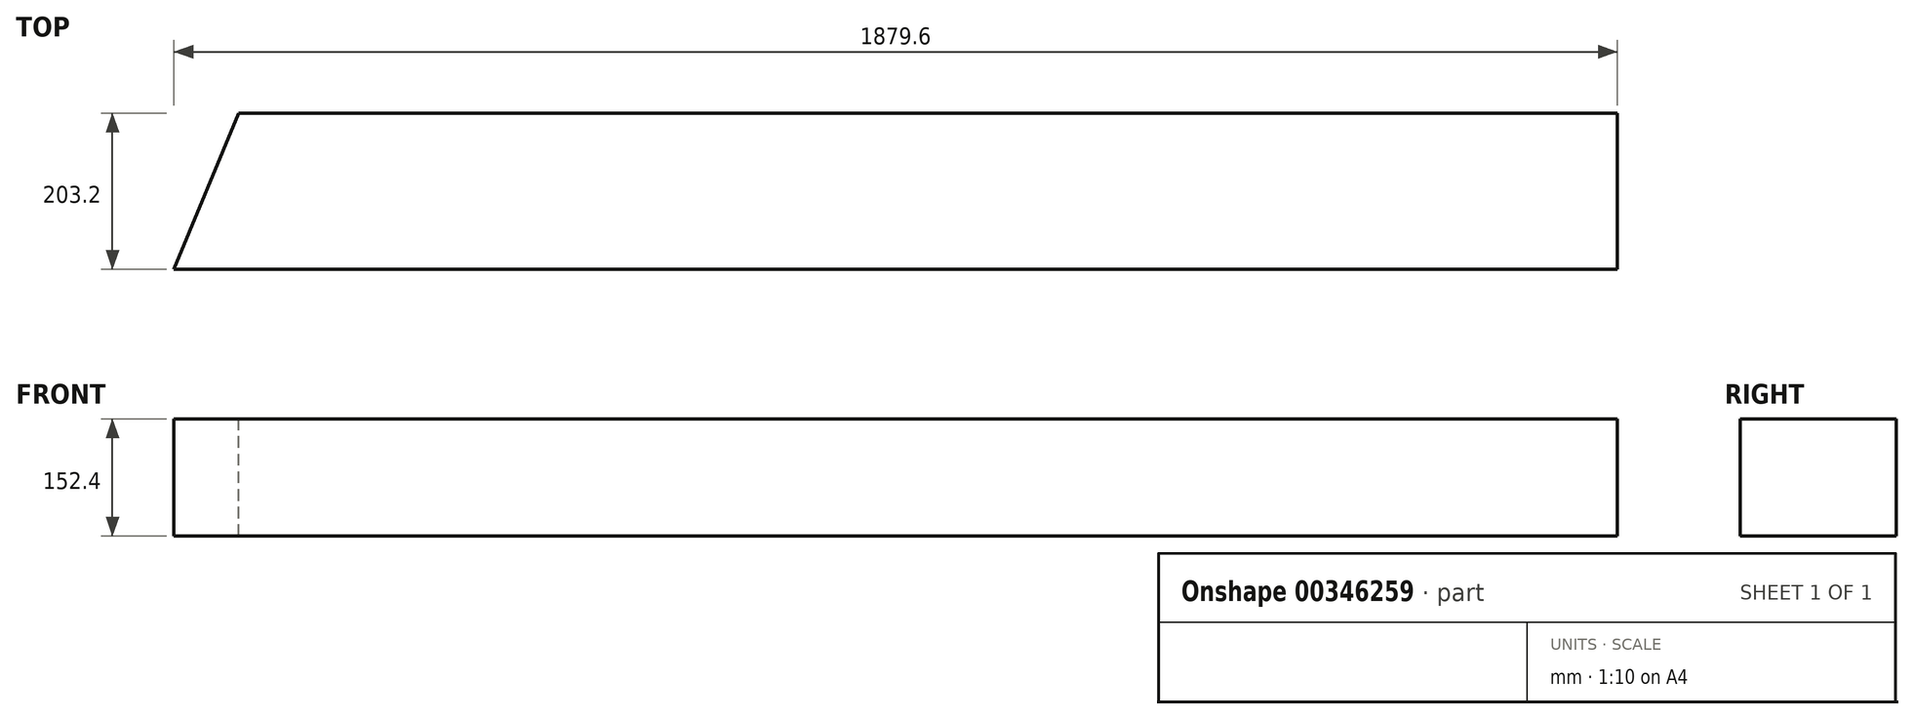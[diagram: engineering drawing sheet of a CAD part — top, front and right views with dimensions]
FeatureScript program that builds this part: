
annotation { "Feature Type Name" : "Feature", "Feature Type Description" : "" }
export const myFeature = defineFeature(function(context is Context, id is Id, definition is map)
    precondition{}
    {
        {
            var Q0;
            Q0=qCreatedBy(makeId("Right.planeOp"),FACE);
            var sketch = newSketch(context, id + "F0", { "sketchPlane" : qUnion([Q0])});
            skLineSegment(sketch, "E0.bottom", {"start": v(-101.6, 76.2) * mm, "end": v(101.6, 76.2) * mm});
            skLineSegment(sketch, "E0.top", {"start": v(-101.6, -76.2) * mm, "end": v(101.6, -76.2) * mm});
            skLineSegment(sketch, "E0.left", {"start": v(-101.6, 76.2) * mm, "end": v(-101.6, -76.2) * mm});
            skLineSegment(sketch, "E0.right", {"start": v(101.6, 76.2) * mm, "end": v(101.6, -76.2) * mm});
            skSolve(sketch);
        }
        {
            var Q0;
            Q0=makeQuery(id+"F0.imprint","IMPRINT",FACE,{"disambiguationData":[TD([[makeQuery(id+"F0.imprint","IMPRINT",EDGE,{"derivedFrom":sQuery(id+"F0.wireOp",EDGE,"E0.bottom")}),-1.0]])]});
            extrude(context, id + "F1", {"entities" : qUnion([Q0]), "endBound" : BoundingType.SYMMETRIC, "depth" : 1879.6 * mm});
        }
        {
            var Q0;
            Q0=makeQuery(id+"F1.opExtrude","SWEPT_FACE",FACE,{"disambiguationData":[OSD([sQuery(id+"F0.wireOp",EDGE,"E0.bottom")])]});
            var sketch = newSketch(context, id + "F2", { "sketchPlane" : qUnion([Q0])});
            skLineSegment(sketch, "E1", {"start": v(-939.8, -101.6) * mm, "end": v(-855.63, 101.6) * mm});
            skLineSegment(sketch, "E2", {"start": v(-855.63, 101.6) * mm, "end": v(-939.8, 101.6) * mm});
            skLineSegment(sketch, "E3", {"start": v(-939.8, 101.6) * mm, "end": v(-939.8, -101.6) * mm});
            skSolve(sketch);
        }
        {
            var Q0;
            Q0 = qSketchRegion(id + "F2", true);
            extrude(context, id + "F3", {"entities" : qUnion([Q0]), "operationType" : NewBodyOperationType.REMOVE, "endBound" : BoundingType.THROUGH_ALL, "oppositeDirection" : true, "depth" : 25.4 * mm});
        }
    });
